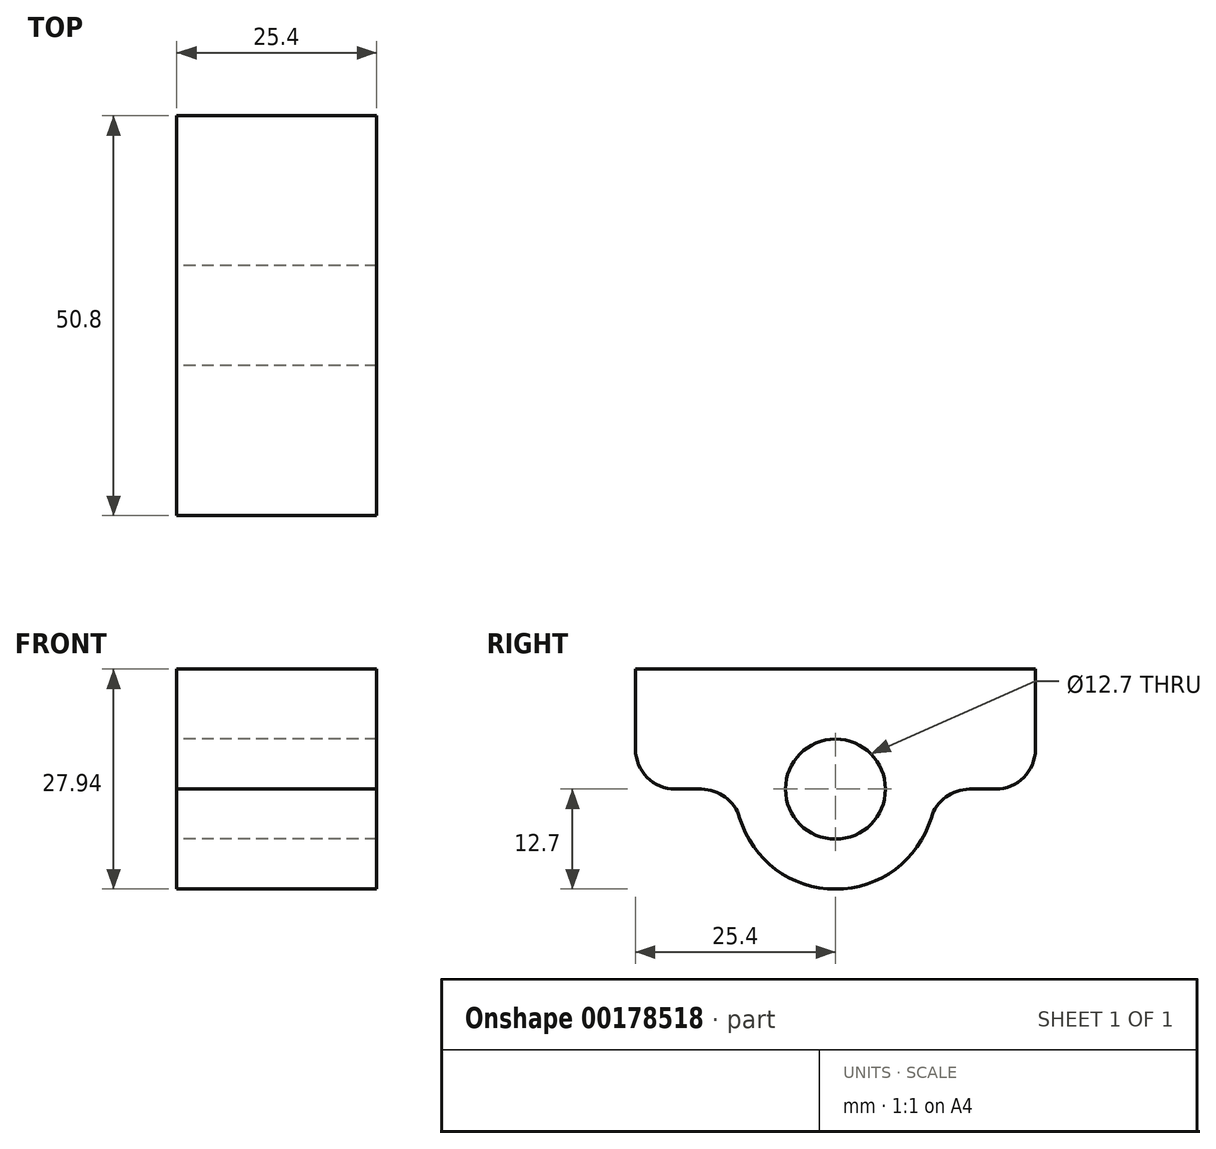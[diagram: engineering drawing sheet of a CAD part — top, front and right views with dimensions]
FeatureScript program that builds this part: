
annotation { "Feature Type Name" : "Feature", "Feature Type Description" : "" }
export const myFeature = defineFeature(function(context is Context, id is Id, definition is map)
    precondition{}
    {
        {
            var Q0;
            Q0=qCreatedBy(makeId("Right.planeOp"),FACE);
            var sketch = newSketch(context, id + "F0", { "sketchPlane" : qUnion([Q0])});
            skCircle(sketch, "E0", {"center": v(0, 0) * mm, "radius": 6.35 * mm});
            skCircle(sketch, "E1.0", {"center": v(0, 0) * mm, "radius": 12.7 * mm});
            skLineSegment(sketch, "E2", {"start": v(-12.7, 0) * mm, "end": v(-25.4, 0) * mm});
            skLineSegment(sketch, "E3", {"start": v(-25.4, 0) * mm, "end": v(-25.4, 15.24) * mm});
            skLineSegment(sketch, "E4", {"start": v(-25.4, 15.24) * mm, "end": v(25.4, 15.24) * mm});
            skLineSegment(sketch, "E5", {"start": v(25.4, 15.24) * mm, "end": v(25.4, 0) * mm});
            skLineSegment(sketch, "E6", {"start": v(25.4, 0) * mm, "end": v(12.7, 0) * mm});
            skSolve(sketch);
        }
        {
            var Q0;
            {var subQ0=sQuery(id+"F0.wireOp",EDGE,"E2");Q0=makeQuery(id+"F0.imprint","IMPRINT",FACE,{"disambiguationData":[TD([[makeQuery(id+"F0.imprint","IMPRINT",EDGE,{"derivedFrom":subQ0}),-1.0]])]});}
            var Q1;
            Q1=makeQuery(id+"F0.imprint","IMPRINT",FACE,{"disambiguationData":[TD([[makeQuery(id+"F0.imprint","IMPRINT",EDGE,{"derivedFrom":sQuery(id+"F0.wireOp",EDGE,"E0")}),-1.0]])]});
            extrude(context, id + "F1", {"entities" : qUnion([Q0, Q1]), "depth" : 25.4 * mm});
        }
        {
            var Q0;
            Q0=makeQuery(id+"F1.opExtrude","SWEPT_EDGE",EDGE,{"disambiguationData":[OSD([sQuery(id+"F0.wireOp",EDGE,"E1.0"),sQuery(id+"F0.wireOp",EDGE,"E2")])]});
            var Q1;
            Q1=makeQuery(id+"F1.opExtrude","SWEPT_EDGE",EDGE,{"disambiguationData":[OSD([sQuery(id+"F0.wireOp",EDGE,"E1.0"),sQuery(id+"F0.wireOp",EDGE,"E6")])]});
            var Q2;
            Q2=makeQuery(id+"F1.opExtrude","SWEPT_EDGE",EDGE,{"disambiguationData":[OSD([sQuery(id+"F0.wireOp",EDGE,"E5"),sQuery(id+"F0.wireOp",EDGE,"E6")])]});
            var Q3;
            Q3=makeQuery(id+"F1.opExtrude","SWEPT_EDGE",EDGE,{"disambiguationData":[OSD([sQuery(id+"F0.wireOp",EDGE,"E2"),sQuery(id+"F0.wireOp",EDGE,"E3")])]});
            fillet(context, id + "F2", {"entities" : qUnion([Q0, Q1, Q2, Q3]), "radius" : 5.08 * mm, "tangentPropagation" : true, "allowEdgeOverflow" : false});
        }
    });
